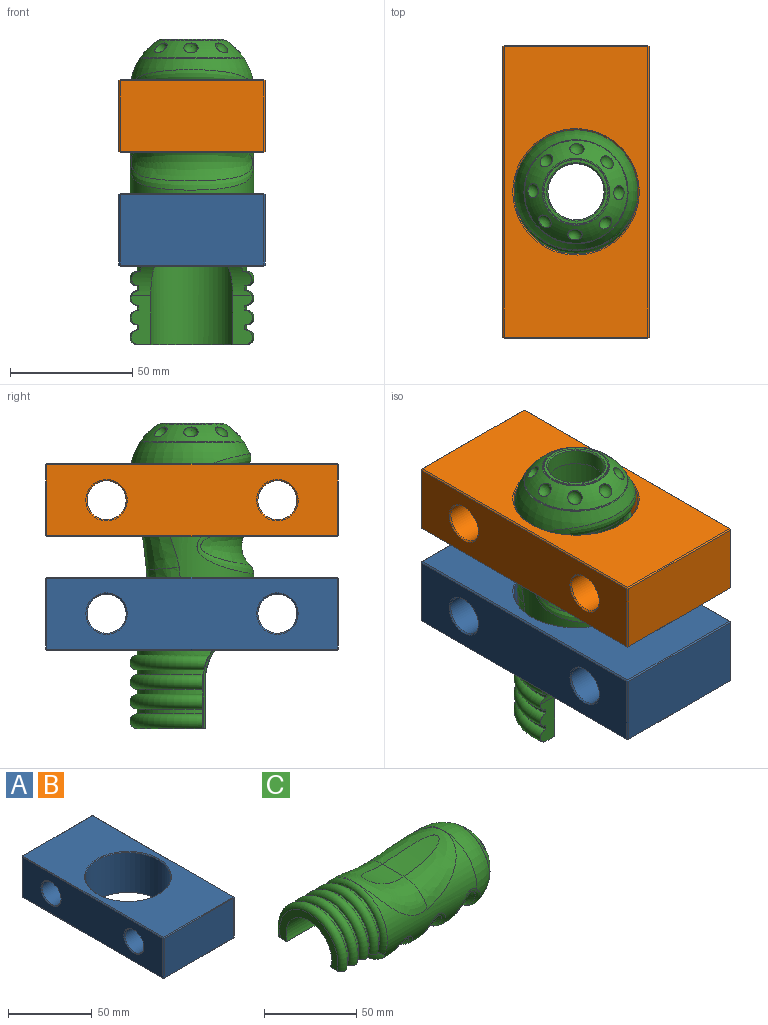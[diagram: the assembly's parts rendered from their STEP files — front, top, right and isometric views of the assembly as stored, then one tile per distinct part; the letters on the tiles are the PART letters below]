
ASSEMBLY  parts=3 mates=2
PART A: 35 faces, bbox 60x120x30 mm
  f0: plane 119x29mm, normal (1,0,0), area 2997mm2, adj f11,f15,f16,f17,f32,f33
  f1: plane 119x29mm, normal (-1,0,0), area 2997mm2, adj f9,f10,f19,f24,f27,f30
  f2: plane 59x29mm, normal (0,1,0), area 1711mm2, adj f11,f14,f18,f19
  f3: plane 59x29mm, normal (0,-1,0), area 1711mm2, adj f16,f25,f26,f30
  f4: plane 119x59mm, normal (0,0,1), area 4913.6mm2, adj f14,f15,f24,f25,f34
  f5: plane 119x59mm, normal (0,0,-1), area 4913.6mm2, adj f17,f18,f26,f27,f31
  f6: cylinder r=25.4mm len=50.8mm, axis (0,0,1), area 4628.2mm2, adj f31,f34
  f7: cylinder r=8mm len=59mm, axis (1,0,0), area 2965.7mm2, adj f9,f32
  f8: cylinder r=8mm len=59mm, axis (1,0,0), area 2965.7mm2, adj f10,f33
  f9: cone r=8mm half-angle=45deg, axis (-1,0,0), area 36.7mm2, adj f1,f7
  f10: cone r=8.5mm half-angle=45deg, axis (-1,0,0), area 36.7mm2, adj f1,f8
  f11: plane 29x0.5mm, normal (0.71,0.71,0), area 20.5mm2, adj f0,f2,f12,f13
  f12: plane 0.5x0.5mm, normal (0.58,0.58,0.58), area 0.2mm2, adj f11,f14,f15
  f13: plane 0.5x0.5mm, normal (0.58,0.58,-0.58), area 0.2mm2, adj f11,f17,f18
  f14: plane 59x0.5mm, normal (0,0.71,0.71), area 41.7mm2, adj f2,f4,f12,f20
  f15: plane 119x0.5mm, normal (0.71,0,0.71), area 84.1mm2, adj f0,f4,f12,f21
  f16: plane 29x0.5mm, normal (0.71,-0.71,0), area 20.5mm2, adj f0,f3,f21,f22
  f17: plane 119x0.5mm, normal (0.71,0,-0.71), area 84.1mm2, adj f0,f5,f13,f22
  f18: plane 59x0.5mm, normal (0,0.71,-0.71), area 41.7mm2, adj f2,f5,f13,f23
  f19: plane 29x0.5mm, normal (-0.71,0.71,0), area 20.5mm2, adj f1,f2,f20,f23
  f20: plane 0.5x0.5mm, normal (-0.58,0.58,0.58), area 0.2mm2, adj f14,f19,f24
  f21: plane 0.5x0.5mm, normal (0.58,-0.58,0.58), area 0.2mm2, adj f15,f16,f25
  f22: plane 0.5x0.5mm, normal (0.58,-0.58,-0.58), area 0.2mm2, adj f16,f17,f26
  f23: plane 0.5x0.5mm, normal (-0.58,0.58,-0.58), area 0.2mm2, adj f18,f19,f27
  f24: plane 119x0.5mm, normal (-0.71,0,0.71), area 84.1mm2, adj f1,f4,f20,f28
  f25: plane 59x0.5mm, normal (0,-0.71,0.71), area 41.7mm2, adj f3,f4,f21,f28
  f26: plane 59x0.5mm, normal (0,-0.71,-0.71), area 41.7mm2, adj f3,f5,f22,f29
  f27: plane 119x0.5mm, normal (-0.71,0,-0.71), area 84.1mm2, adj f1,f5,f23,f29
  f28: plane 0.5x0.5mm, normal (-0.58,-0.58,0.58), area 0.2mm2, adj f24,f25,f30
  f29: plane 0.5x0.5mm, normal (-0.58,-0.58,-0.58), area 0.2mm2, adj f26,f27,f30
  f30: plane 29x0.5mm, normal (-0.71,-0.71,0), area 20.5mm2, adj f1,f3,f28,f29
  f31: cone r=25.9mm half-angle=45deg, axis (0,0,-1), area 114mm2, adj f5,f6
  f32: cone r=8.5mm half-angle=45deg, axis (1,0,0), area 36.7mm2, adj f0,f7
  f33: cone r=8mm half-angle=45deg, axis (1,0,0), area 36.7mm2, adj f0,f8
  f34: cone r=25.4mm half-angle=45deg, axis (0,0,1), area 114mm2, adj f4,f6
PART B: same geometry as A
PART C: 45 faces, bbox 125x88.7x102.2 mm
  f0: plane 26.23x26.23mm, normal (1,0,0), area 88.1mm2, adj f29,f44
  f1: torus R=0.9mm, axis (-1,0,0), area 1649mm2, adj f3,f34,f41
  f2: torus R=0.9mm, axis (-1,0,0), area 932.3mm2, adj f8,f12,f13,f14,f15,f16,f17,f18
  f3: cylinder r=25.4mm len=68.84mm, axis (-1,0,0), area 3455.7mm2, adj f1,f5,f28,f33,f35,f36,f39,f40
  f4: plane 20x8.13mm, normal (0,0,-1), area 140.5mm2, adj f5,f7,f11,f20,f21,f23,f24,f25
  f5: cylinder r=20.4mm len=49.46mm, axis (0,1,0), area 611.3mm2, adj f3,f4,f6,f11,f21,f22,f26,f27
  f6: plane 20x8.13mm, normal (0,0,-1), area 140.5mm2, adj f5,f7,f11,f20,f21,f23,f24,f25
  f7: plane 44.8x27.4mm, normal (-1,0,0), area 356.6mm2, adj f4,f6,f11,f23
  f8: plane 27.5x27.5mm, normal (1,0,0), area 37.9mm2, adj f2,f43
  f9: cylinder r=11.5mm len=23mm, axis (1,0,0), area 469.7mm2, adj f10,f29
  f10: plane 35x35mm, normal (-1,0,0), area 546.6mm2, adj f9,f11
  f11: cylinder r=17.5mm len=118mm, axis (-1,0,0), area 11392mm2, adj f4,f5,f6,f7,f10
  f12: sphere r=3mm, area 44.9mm2, adj f2
  f13: sphere r=3mm, area 44.9mm2, adj f2
  f14: sphere r=3mm, area 44.9mm2, adj f2
  f15: sphere r=3mm, area 44.9mm2, adj f2
  f16: sphere r=3mm, area 44.9mm2, adj f2
  f17: sphere r=3mm, area 44.9mm2, adj f2
  f18: sphere r=3mm, area 44.9mm2, adj f2
  f19: sphere r=3mm, area 45mm2, adj f2
  f20: torus R=22.4mm, axis (-1,0,0), area 814.7mm2, adj f4,f6,f24,f25
  f21: torus R=22.4mm, axis (-1,0,0), area 815.1mm2, adj f4,f5,f6,f25,f26
  f22: torus R=22.4mm, axis (-1,0,0), area 841.4mm2, adj f5,f26,f27
  f23: torus R=22.4mm, axis (-1,0,0), area 814.8mm2, adj f4,f6,f7,f24
  f24: cylinder r=22.4mm len=44.8mm, axis (-1,0,0), area 160.9mm2, adj f4,f6,f20,f23
  f25: cylinder r=22.4mm len=44.8mm, axis (-1,0,0), area 160.9mm2, adj f4,f6,f20,f21
  f26: cylinder r=22.4mm len=44.8mm, axis (-1,0,0), area 161.9mm2, adj f5,f21,f22
  f27: cylinder r=22.4mm len=44.8mm, axis (-1,0,0), area 174.6mm2, adj f5,f22,f28
  f28: torus R=22.4mm, axis (-1,0,0), area 455mm2, adj f3,f5,f27
  f29: cone r=11.5mm half-angle=45deg, axis (1,0,0), area 52.2mm2, adj f0,f9
  f30: bspline ~84.63x84.63mm, area 947.6mm2, adj f33,f34
  f31: bspline ~86.66x86.66mm, area 849.4mm2, adj f36
  f32: bspline ~88.7x88.7mm, area 694.4mm2, adj f35
  f33: bspline ~50.83x26.58mm, area 326.5mm2, adj f3,f30,f34
  f34: bspline ~50.78x24.59mm, area 359.2mm2, adj f1,f30,f33
  f35: bspline ~49.05x20.93mm, area 418.6mm2, adj f3,f32
  f36: bspline ~50.53x22.82mm, area 520.1mm2, adj f3,f31
  f37: cylinder r=145mm len=33.82mm, axis (0,1,0), area 466.5mm2, adj f38,f39
  f38: cylinder r=40mm len=21.62mm, axis (0,1,0), area 320.7mm2, adj f37,f40
  f39: bspline ~50.13x43.84mm, area 1416.6mm2, adj f3,f37,f40
  f40: bspline ~50.07x34.26mm, area 1286mm2, adj f3,f38,f39
  f41: cone r=20.75mm half-angle=75deg, axis (-1,0,0), area 81.4mm2, adj f1,f42
  f42: cone r=26.08mm half-angle=75deg, axis (1,0,0), area 56.4mm2, adj f2,f41
  f43: cone r=14.56mm half-angle=15deg, axis (1,0,0), area 17.3mm2, adj f8,f44
  f44: cone r=13.25mm half-angle=15deg, axis (-1,0,0), area 42.9mm2, adj f0,f43
PLACE A t=(-24.34,-69.43,-101.93)mm
PLACE B rot(axis=(0,0,1),180deg) t=(-24.34,-69.43,-55.45)mm
PLACE C rot(axis=(-0.58,-0.57,-0.58),120.8deg) t=(-24.34,-69.43,-134.01)mm
MATE planar B.f0 <-> A.f1  axis (-1,0,0) through (-54.34,-69.43,-40.45)mm
MATE cylindrical A.f6 <-> C.f1  axis (0,0,1) through (-24.34,-69.43,-72.43)mm
